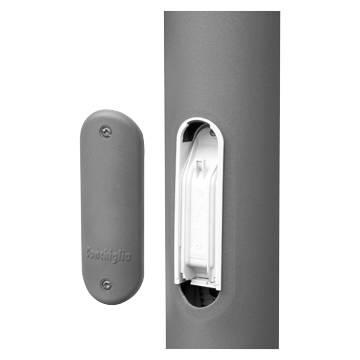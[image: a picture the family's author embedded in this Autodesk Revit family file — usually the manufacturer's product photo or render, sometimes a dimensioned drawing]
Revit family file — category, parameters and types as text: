
# Revit family: Lighting-UrbanSystem-GEWISS-URBAN[O3]-POLES
name_source: partatom
category: Apparecchi per illuminazione
units: mm (PartAtom-declared; Revit-internal decimal feet)

## family parameters
Condiviso = No
Host = Superficie
Numero OmniClass = 23.80.00.00
Punto di calcolo locali = Sì
Quota connettore circolare = Usa diametro
Sorgente d'illuminazione = No
Taglio con vuoti quando caricato = No
Tipo di parte = Normale
Titolo OmniClass = Electric Power and Lighting

## types (7) — shared parameters
Altezza palo = 8800 mm  [stored 28.8714 ft]
Catalogue = LIGHTING
Diametro = 60 mm  [stored 0.19685 ft]
Diametro inferiore = 148 mm  [stored 0.485564 ft]
Electrocod = 240
Finishing = Painted
IDF = 5d5d73d8-af2e-4a7e-bae8-de50127309a4
IDT = fb51b8d7-080d-47f3-85ad-856ae9a19558
Immagine tipo = GW84096.jpg
Palo = <Per categoria>
Produttore = GEWISS S.p.A.
Prospetto di default = 1219 mm
SEO = Pole
Technical sheet = https://www.gewiss.com
Top diameter (mm) = 60
URL = https://www.gewiss.com
Version file RFA = 20.11

## per-type parameters (varying)
| type | Base diameter (mm) | Catalogue Range | Colour | Descrizione | EAN code | Material | Modello | Planting (m) | Total length (m) | Type: | Weight (kg) | Weight (kg): |
| GW87691 - PAINTED CYLINDRICAL POLE D.60MM 3,5M GR. | 102 |  | Graphite grey | PAINTED CYLINDRICAL POLE D.60MM 3,5M GR. |  |  | GW87691 | 0,5 | 4 | Cylindrical |  | 31 |
| GW87692B - PAINTED CYLINDRICAL POLE.D.60MM 4M BLUE | 102 |  | BlueGreen | PAINTED CYLINDRICAL POLE.D.60MM 4M BLUE |  |  | GW87692B | 0,5 | 4,5 | Cylindrical |  | 35 |
| GW87592 - STREET CONICAL POLE 8,8m GRAPHITE GREY | 148 | STREET [O3] | Graphite grey | STREET CONICAL POLE 8,8m GRAPHITE GREY | 8011564782587 | Galvanised steel | GW87592 | 0,8 | 8,8 | Conical | 91 | 91 |
| GW87692 - PAINTED CYLINDRICAL POLE.D.60MM 4M GR. | 102 |  | Graphite grey | PAINTED CYLINDRICAL POLE.D.60MM 4M GR. |  |  | GW87692 | 0,5 | 4,5 | Cylindrical |  | 35 |
| GW87591 - STREET CONICAL POLE 6,8m GRAPHITE GREY | 128 | STREET [O3] | Graphite grey | STREET CONICAL POLE 6,8m GRAPHITE GREY | 8011564782570 | Galvanised steel | GW87591 | 0,8 | 6,8 | Conical | 48 | 48 |
| GW87691B - PAINTED CYLINDRICAL POLE D.60MM 3,5M BL. | 102 |  | BlueGreen | PAINTED CYLINDRICAL POLE D.60MM 3,5M BL. |  |  | GW87691B | 0,5 | 4 | Cylindrical |  | 31 |
| GW87593 - STREET CONICAL POLE 9,8m GRAPHITE GREY | 158 | STREET [O3] | Graphite grey | STREET CONICAL POLE 9,8m GRAPHITE GREY | 8011564782594 | Galvanised steel | GW87593 | 0,8 | 9,8 | Conical | 107 | 107 |

note: [stored X ft] marks values corroborated as IEEE doubles in the binary element streams (Revit-internal decimal feet)

## geometry (parser evidence)
native form markers: Blend x2
no freeform markers — native parametric forms only
